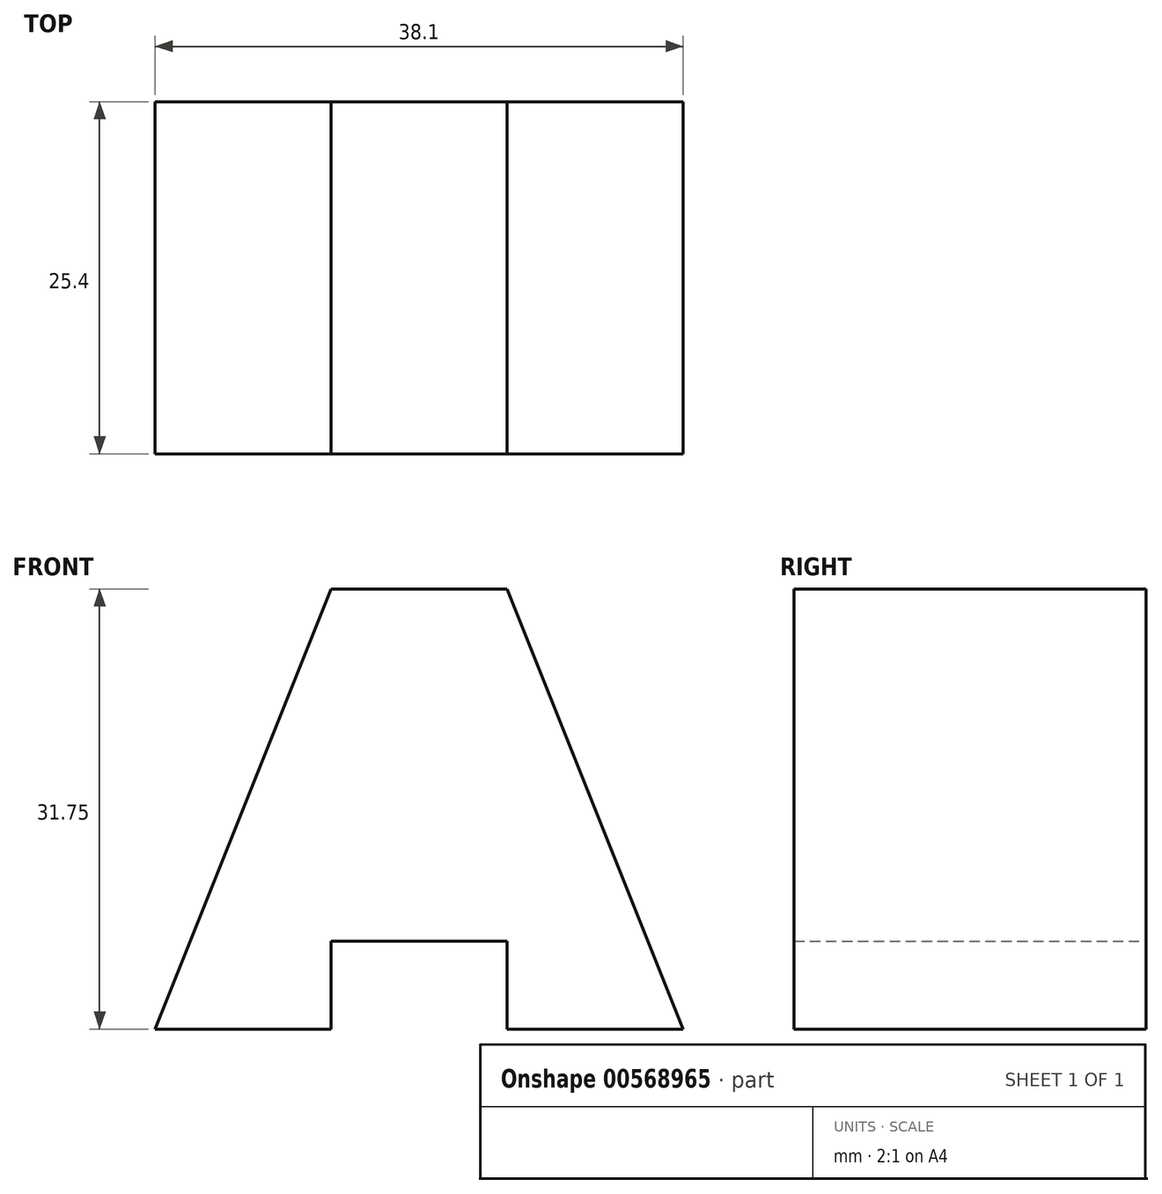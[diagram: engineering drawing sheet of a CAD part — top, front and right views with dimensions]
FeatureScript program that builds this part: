
annotation { "Feature Type Name" : "Feature", "Feature Type Description" : "" }
export const myFeature = defineFeature(function(context is Context, id is Id, definition is map)
    precondition{}
    {
        {
            var Q0;
            Q0=qCreatedBy(makeId("Front.planeOp"),FACE);
            var sketch = newSketch(context, id + "F0", { "sketchPlane" : qUnion([Q0])});
            skLineSegment(sketch, "E0", {"start": v(0, 0) * mm, "end": v(12.7, 0) * mm});
            skLineSegment(sketch, "E1", {"start": v(12.7, 0) * mm, "end": v(12.7, 6.35) * mm});
            skLineSegment(sketch, "E2", {"start": v(12.7, 6.35) * mm, "end": v(25.4, 6.35) * mm});
            skLineSegment(sketch, "E3", {"start": v(25.4, 6.35) * mm, "end": v(25.4, 0) * mm});
            skLineSegment(sketch, "E4", {"start": v(25.4, 0) * mm, "end": v(38.1, 0) * mm});
            skLineSegment(sketch, "E5", {"start": v(0, 0) * mm, "end": v(12.7, 31.75) * mm});
            skLineSegment(sketch, "E6", {"start": v(38.1, 0) * mm, "end": v(25.4, 31.75) * mm});
            skLineSegment(sketch, "E7", {"start": v(12.7, 31.75) * mm, "end": v(25.4, 31.75) * mm});
            skSolve(sketch);
        }
        {
            var Q0;
            Q0 = qSketchRegion(id + "F0", true);
            extrude(context, id + "F1", {"entities" : qUnion([Q0]), "depth" : 25.4 * mm, "offsetDistance" : 25.4 * mm});
        }
    });
